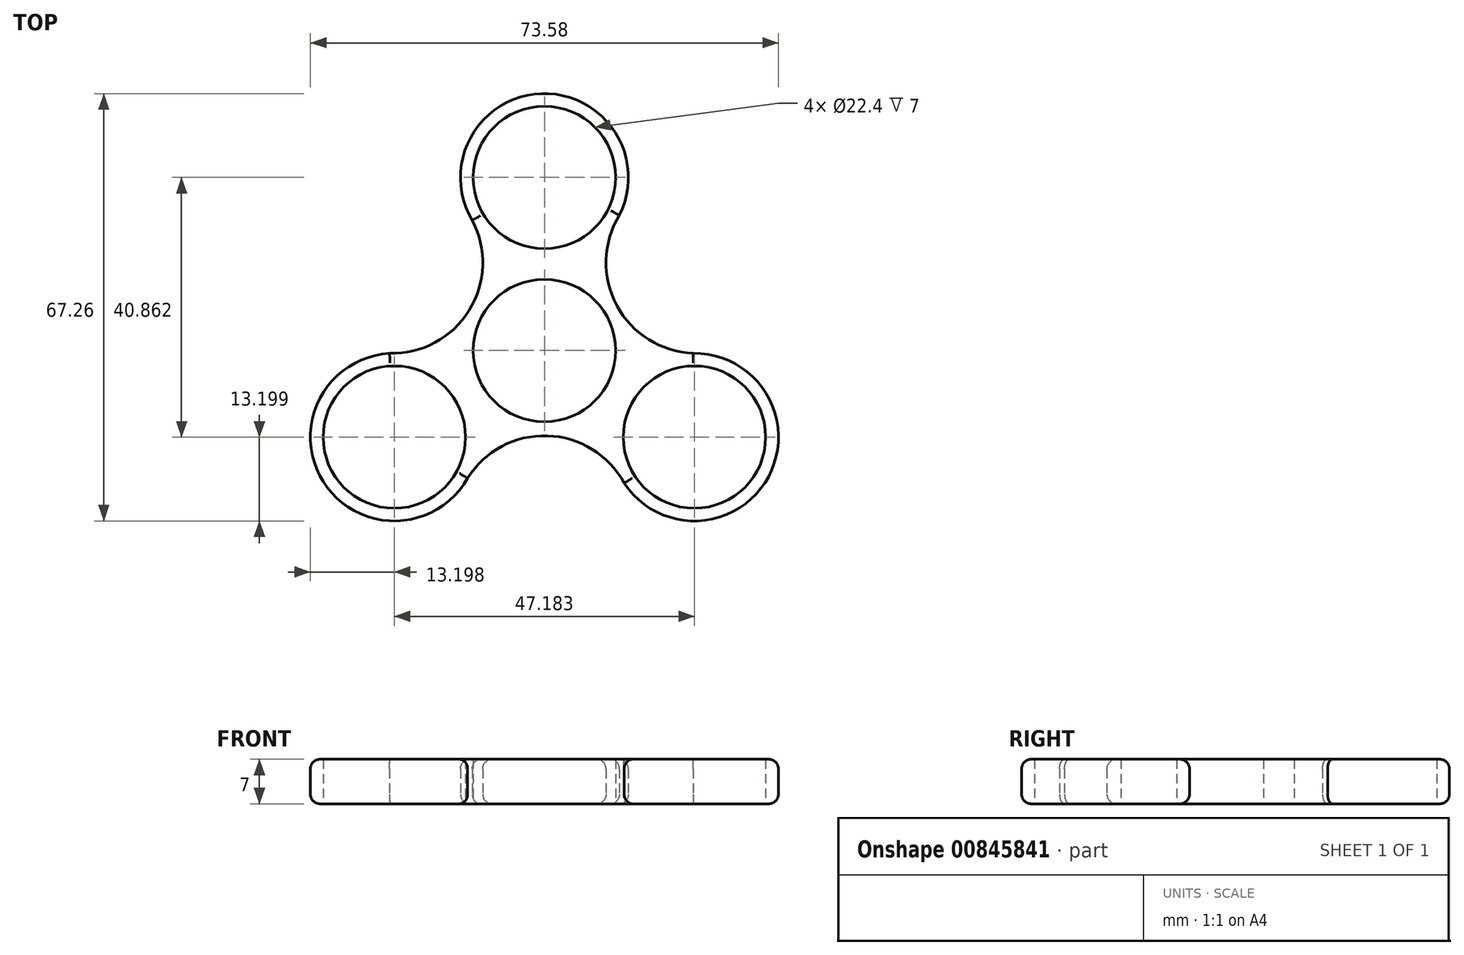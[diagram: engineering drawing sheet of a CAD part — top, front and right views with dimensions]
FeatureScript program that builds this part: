
annotation { "Feature Type Name" : "Feature", "Feature Type Description" : "" }
export const myFeature = defineFeature(function(context is Context, id is Id, definition is map)
    precondition{}
    {
        {
            var Q0;
            Q0=qCreatedBy(makeId("Top.planeOp"),FACE);
            var sketch = newSketch(context, id + "F0", { "sketchPlane" : qUnion([Q0])});
            skCircle(sketch, "E0", {"center": v(0, 0) * mm, "radius": 11.2 * mm});
            skArc(sketch, "E1", {"start": v(11.24, 20.32) * mm, "mid": v(0.1, 40.44) * mm, "end": v(-11.35, 20.5) * mm});
            skCircle(sketch, "E2", {"center": v(0, 27.24) * mm, "radius": 11.2 * mm});
            skCircle(sketch, "E3.1.0", {"center": v(-23.6, -13.62) * mm, "radius": 11.2 * mm});
            skArc(sketch, "E3.1.1", {"start": v(-23.22, -0.43) * mm, "mid": v(-35.07, -20.13) * mm, "end": v(-12.08, -20.07) * mm});
            skCircle(sketch, "E3.2.0", {"center": v(23.6, -13.62) * mm, "radius": 11.2 * mm});
            skArc(sketch, "E3.2.1", {"start": v(11.98, -19.9) * mm, "mid": v(34.97, -20.3) * mm, "end": v(23.42, -0.42) * mm});
            skArc(sketch, "E4", {"start": v(11.78, 21.3) * mm, "mid": v(11.38, 7.1) * mm, "end": v(23.42, -0.42) * mm});
            skArc(sketch, "E5.1.0", {"start": v(-24.33, -0.44) * mm, "mid": v(-11.84, 6.3) * mm, "end": v(-11.35, 20.5) * mm});
            skArc(sketch, "E5.2.0", {"start": v(12.55, -20.85) * mm, "mid": v(0.46, -13.4) * mm, "end": v(-12.08, -20.07) * mm});
            skSolve(sketch);
        }
        {
            var Q0;
            Q0=makeQuery(id+"F0.imprint","IMPRINT",FACE,{"disambiguationData":[TD([[makeQuery(id+"F0.imprint","IMPRINT",EDGE,{"derivedFrom":sQuery(id+"F0.wireOp",EDGE,"E0")}),-1.0]])]});
            extrude(context, id + "F1", {"entities" : qUnion([Q0]), "depth" : 7 * mm, "offsetDistance" : 25 * mm});
        }
        {
            var Q0;
            Q0=makeQuery(id+"F1.opExtrude","CAP_EDGE",EDGE,{"disambiguationData":[OSD([sQuery(id+"F0.wireOp",EDGE,"E3.1.1")])],"isStart":false});
            var Q1;
            Q1=makeQuery(id+"F1.opExtrude","CAP_EDGE",EDGE,{"disambiguationData":[OSD([sQuery(id+"F0.wireOp",EDGE,"E5.2.0")])],"isStart":false});
            var Q2;
            Q2=makeQuery(id+"F1.opExtrude","CAP_EDGE",EDGE,{"disambiguationData":[OSD([sQuery(id+"F0.wireOp",EDGE,"E5.1.0")])],"isStart":false});
            var Q3;
            Q3=makeQuery(id+"F1.opExtrude","CAP_EDGE",EDGE,{"disambiguationData":[OSD([sQuery(id+"F0.wireOp",EDGE,"E1")])],"isStart":false});
            var Q4;
            Q4=makeQuery(id+"F1.opExtrude","CAP_EDGE",EDGE,{"disambiguationData":[OSD([sQuery(id+"F0.wireOp",EDGE,"E4")])],"isStart":false});
            var Q5;
            Q5=makeQuery(id+"F1.opExtrude","CAP_EDGE",EDGE,{"disambiguationData":[OSD([sQuery(id+"F0.wireOp",EDGE,"E3.2.1")])],"isStart":false});
            var Q6;
            Q6=makeQuery(id+"F1.opExtrude","CAP_EDGE",EDGE,{"disambiguationData":[OSD([sQuery(id+"F0.wireOp",EDGE,"E3.1.1")])],"isStart":true});
            var Q7;
            Q7=makeQuery(id+"F1.opExtrude","CAP_EDGE",EDGE,{"disambiguationData":[OSD([sQuery(id+"F0.wireOp",EDGE,"E5.2.0")])],"isStart":true});
            var Q8;
            Q8=makeQuery(id+"F1.opExtrude","CAP_EDGE",EDGE,{"disambiguationData":[OSD([sQuery(id+"F0.wireOp",EDGE,"E5.1.0")])],"isStart":true});
            var Q9;
            Q9=makeQuery(id+"F1.opExtrude","CAP_EDGE",EDGE,{"disambiguationData":[OSD([sQuery(id+"F0.wireOp",EDGE,"E1")])],"isStart":true});
            var Q10;
            Q10=makeQuery(id+"F1.opExtrude","CAP_EDGE",EDGE,{"disambiguationData":[OSD([sQuery(id+"F0.wireOp",EDGE,"E4")])],"isStart":true});
            var Q11;
            Q11=makeQuery(id+"F1.opExtrude","CAP_EDGE",EDGE,{"disambiguationData":[OSD([sQuery(id+"F0.wireOp",EDGE,"E3.2.1")])],"isStart":true});
            fillet(context, id + "F2", {"entities" : qUnion([Q0, Q1, Q2, Q3, Q4, Q5, Q6, Q7, Q8, Q9, Q10, Q11]), "radius" : 1.5 * mm, "tangentPropagation" : true, "allowEdgeOverflow" : false});
        }
    });
